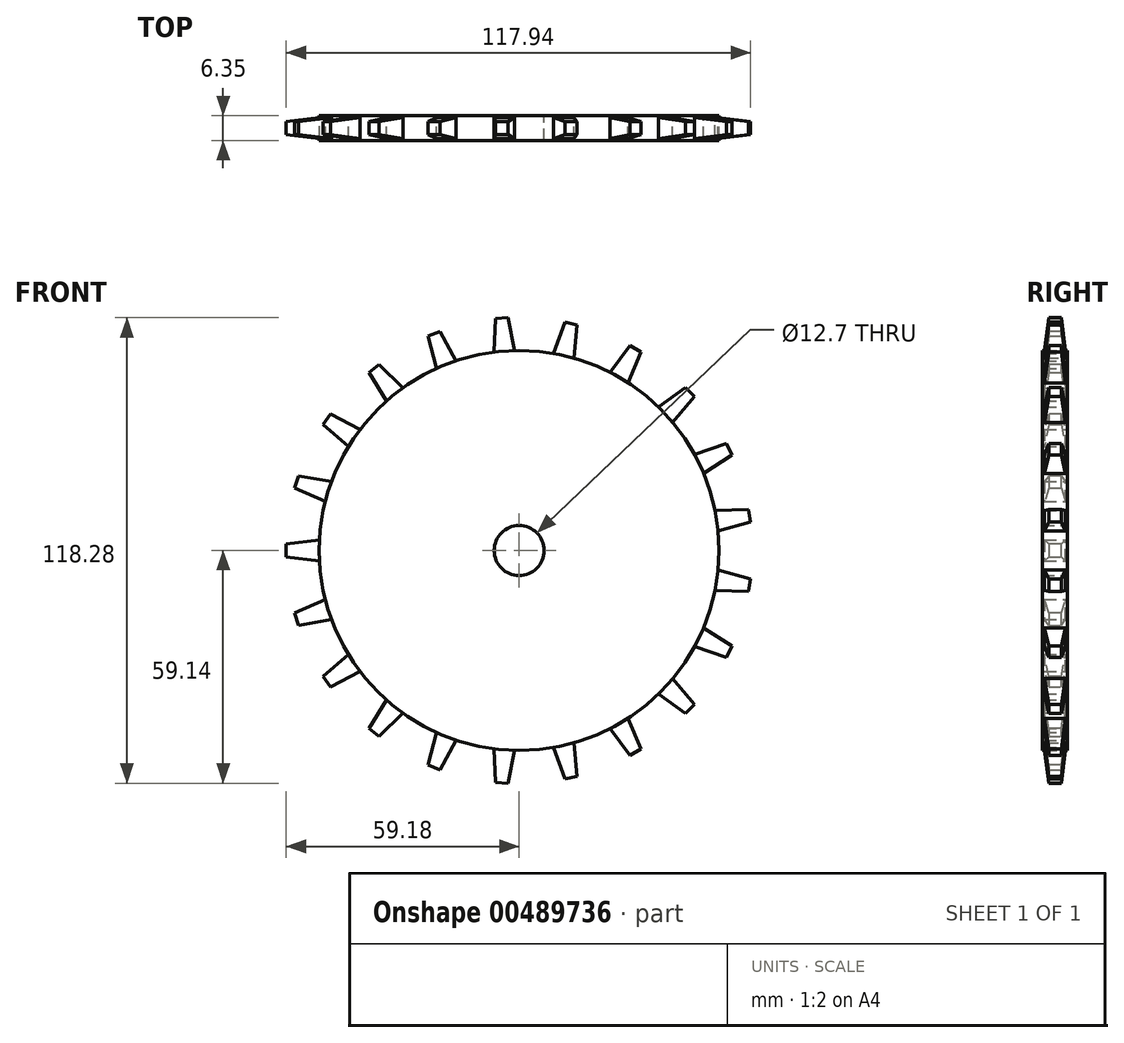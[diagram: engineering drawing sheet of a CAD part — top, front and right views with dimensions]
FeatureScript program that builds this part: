
annotation { "Feature Type Name" : "Feature", "Feature Type Description" : "" }
export const myFeature = defineFeature(function(context is Context, id is Id, definition is map)
    precondition{}
    {
        {
            var Q0;
            Q0=qCreatedBy(makeId("Front.planeOp"),FACE);
            var sketch = newSketch(context, id + "F0", { "sketchPlane" : qUnion([Q0])});
            skCircle(sketch, "E0", {"center": v(0, 0) * mm, "radius": 50.8 * mm});
            skCircle(sketch, "E1", {"center": v(0, 0) * mm, "radius": 6.35 * mm});
            skLineSegment(sketch, "E2", {"start": v(-57.15, 0) * mm, "end": v(-57.15, 3.8) * mm});
            skLineSegment(sketch, "E3", {"start": v(-57.15, -3.81) * mm, "end": v(-57.15, 0) * mm});
            skLineSegment(sketch, "E4.1.2", {"start": v(-39.4, 41.4) * mm, "end": v(-36.63, 44.03) * mm});
            skLineSegment(sketch, "E4.1.3", {"start": v(-42.15, 38.78) * mm, "end": v(-39.4, 41.4) * mm});
            skLineSegment(sketch, "E4.2.2", {"start": v(2.85, 57.08) * mm, "end": v(6.65, 56.89) * mm});
            skLineSegment(sketch, "E4.2.3", {"start": v(-0.96, 57.27) * mm, "end": v(2.85, 57.08) * mm});
            skLineSegment(sketch, "E4.3.2", {"start": v(43.32, 37.28) * mm, "end": v(45.8, 34.4) * mm});
            skLineSegment(sketch, "E4.3.3", {"start": v(40.83, 40.17) * mm, "end": v(43.32, 37.28) * mm});
            skLineSegment(sketch, "E4.4.2", {"start": v(56.87, -5.7) * mm, "end": v(56.49, -9.48) * mm});
            skLineSegment(sketch, "E4.4.3", {"start": v(57.25, -1.9) * mm, "end": v(56.87, -5.7) * mm});
            skLineSegment(sketch, "E4.5.2", {"start": v(35.07, -45.12) * mm, "end": v(32.06, -47.46) * mm});
            skLineSegment(sketch, "E4.5.3", {"start": v(38.08, -42.78) * mm, "end": v(35.07, -45.12) * mm});
            skLineSegment(sketch, "E4.6.2", {"start": v(-8.52, -56.51) * mm, "end": v(-12.29, -55.94) * mm});
            skLineSegment(sketch, "E4.6.3", {"start": v(-4.75, -57.08) * mm, "end": v(-8.52, -56.51) * mm});
            skLineSegment(sketch, "E4.7.2", {"start": v(-46.81, -32.78) * mm, "end": v(-49, -29.66) * mm});
            skLineSegment(sketch, "E4.7.3", {"start": v(-44.63, -35.9) * mm, "end": v(-46.81, -32.78) * mm});
            skSolve(sketch);
        }
        {
            var Q0;
            Q0 = qSketchRegion(id + "F0", true);
            var Q1;
            {var subQ0=sQuery(id+"F0.wireOp",EDGE,"E4.7.0");var subQ1=sQuery(id+"F0.wireOp",EDGE,"E1");var subQ2=makeQuery(id+"F0.imprint","INTERSECT",VERTEX,{"derivedFrom":[subQ1,subQ0]});Q1=makeQuery(id+"F0.imprint","IMPRINT",FACE,{"disambiguationData":[TD([[makeQuery(id+"F0.imprint","IMPRINT",EDGE,{"disambiguationData":[TD([[subQ2,-1.0]])],"derivedFrom":subQ1}),-1.0]])]});}
            var Q2;
            {var subQ0=sQuery(id+"F0.wireOp",EDGE,"55mzpF7p-MuUW-aDjL-x8Cu-YddlOPHiesim");var subQ1=sQuery(id+"F0.wireOp",EDGE,"E1");var subQ2=makeQuery(id+"F0.imprint","INTERSECT",VERTEX,{"derivedFrom":[subQ1,subQ0]});Q2=makeQuery(id+"F0.imprint","IMPRINT",FACE,{"disambiguationData":[TD([[makeQuery(id+"F0.imprint","IMPRINT",EDGE,{"disambiguationData":[TD([[subQ2,-1.0]])],"derivedFrom":subQ1}),-1.0]])]});}
            var Q3;
            {var subQ0=sQuery(id+"F0.wireOp",EDGE,"E4.1.0");var subQ1=sQuery(id+"F0.wireOp",EDGE,"E1");var subQ2=makeQuery(id+"F0.imprint","INTERSECT",VERTEX,{"derivedFrom":[subQ1,subQ0]});Q3=makeQuery(id+"F0.imprint","IMPRINT",FACE,{"disambiguationData":[TD([[makeQuery(id+"F0.imprint","IMPRINT",EDGE,{"disambiguationData":[TD([[subQ2,-1.0]])],"derivedFrom":subQ1}),-1.0]])]});}
            var Q4;
            {var subQ0=sQuery(id+"F0.wireOp",EDGE,"E4.2.0");var subQ1=sQuery(id+"F0.wireOp",EDGE,"E1");var subQ2=makeQuery(id+"F0.imprint","INTERSECT",VERTEX,{"derivedFrom":[subQ1,subQ0]});Q4=makeQuery(id+"F0.imprint","IMPRINT",FACE,{"disambiguationData":[TD([[makeQuery(id+"F0.imprint","IMPRINT",EDGE,{"disambiguationData":[TD([[subQ2,-1.0]])],"derivedFrom":subQ1}),-1.0]])]});}
            var Q5;
            {var subQ0=sQuery(id+"F0.wireOp",EDGE,"E4.4.1");var subQ1=sQuery(id+"F0.wireOp",EDGE,"E1");var subQ2=makeQuery(id+"F0.imprint","INTERSECT",VERTEX,{"derivedFrom":[subQ1,subQ0]});Q5=makeQuery(id+"F0.imprint","IMPRINT",FACE,{"disambiguationData":[TD([[makeQuery(id+"F0.imprint","IMPRINT",EDGE,{"disambiguationData":[TD([[subQ2,1.0]])],"derivedFrom":subQ1}),-1.0]])]});}
            var Q6;
            {var subQ0=sQuery(id+"F0.wireOp",EDGE,"E4.4.0");var subQ1=sQuery(id+"F0.wireOp",EDGE,"E1");var subQ2=makeQuery(id+"F0.imprint","INTERSECT",VERTEX,{"derivedFrom":[subQ1,subQ0]});Q6=makeQuery(id+"F0.imprint","IMPRINT",FACE,{"disambiguationData":[TD([[makeQuery(id+"F0.imprint","IMPRINT",EDGE,{"disambiguationData":[TD([[subQ2,-1.0]])],"derivedFrom":subQ1}),-1.0]])]});}
            var Q7;
            {var subQ0=sQuery(id+"F0.wireOp",EDGE,"E4.5.0");var subQ1=sQuery(id+"F0.wireOp",EDGE,"E1");var subQ2=makeQuery(id+"F0.imprint","INTERSECT",VERTEX,{"derivedFrom":[subQ1,subQ0]});Q7=makeQuery(id+"F0.imprint","IMPRINT",FACE,{"disambiguationData":[TD([[makeQuery(id+"F0.imprint","IMPRINT",EDGE,{"disambiguationData":[TD([[subQ2,-1.0]])],"derivedFrom":subQ1}),-1.0]])]});}
            var Q8;
            {var subQ0=sQuery(id+"F0.wireOp",EDGE,"E4.6.0");var subQ1=sQuery(id+"F0.wireOp",EDGE,"E1");var subQ2=makeQuery(id+"F0.imprint","INTERSECT",VERTEX,{"derivedFrom":[subQ1,subQ0]});Q8=makeQuery(id+"F0.imprint","IMPRINT",FACE,{"disambiguationData":[TD([[makeQuery(id+"F0.imprint","IMPRINT",EDGE,{"disambiguationData":[TD([[subQ2,-1.0]])],"derivedFrom":subQ1}),-1.0]])]});}
            extrude(context, id + "F1", {"entities" : qUnion([Q0, Q1, Q2, Q3, Q4, Q5, Q6, Q7, Q8]), "depth" : 6.35 * mm});
        }
        {
            var Q0;
            Q0=qCreatedBy(makeId("Right.planeOp"),FACE);
            cPlane(context, id + "F2", {"entities" : qUnion([Q0]), "cplaneType" : CPlaneType.OFFSET, "offset" : 46.48 * mm, "oppositeDirection" : true, "width" : 152.4 * mm, "height" : 152.4 * mm});
        }
        {
            var Q0;
            Q0=qCreatedBy(id+"F2.planeOp",FACE);
            var sketch = newSketch(context, id + "F3", { "sketchPlane" : qUnion([Q0])});
            skLineSegment(sketch, "E5", {"start": v(-6.35, 0) * mm, "end": v(-6.35, 3.17) * mm});
            skLineSegment(sketch, "E6", {"start": v(-6.35, 3.17) * mm, "end": v(0, 3.17) * mm});
            skLineSegment(sketch, "E7", {"start": v(0, 3.17) * mm, "end": v(0, -3.18) * mm});
            skLineSegment(sketch, "E8", {"start": v(0, -3.18) * mm, "end": v(-6.35, -3.18) * mm});
            skLineSegment(sketch, "E9", {"start": v(-6.35, -3.18) * mm, "end": v(-6.35, 0) * mm});
            skSolve(sketch);
        }
        {
            var Q0;
            Q0=makeQuery(id+"F3.imprint","IMPRINT",FACE,{"disambiguationData":[TD([[makeQuery(id+"F3.imprint","IMPRINT",EDGE,{"derivedFrom":sQuery(id+"F3.wireOp",EDGE,"E5")}),-1.0]])]});
            extrude(context, id + "F4", {"entities" : qUnion([Q0]), "operationType" : NewBodyOperationType.ADD, "oppositeDirection" : true, "depth" : 12.7 * mm, "hasDraft" : true, "draftAngle" : 7 * degree, "draftPullDirection" : true});
        }
        {
            var Q0;
            Q0=qCreatedBy(makeId("Right.planeOp"),FACE);
            var sketch = newSketch(context, id + "F5", { "sketchPlane" : qUnion([Q0])});
            skLineSegment(sketch, "E10", {"start": v(0, 0) * mm, "end": v(-61.18, 0) * mm});
            skSolve(sketch);
        }
        {
            var Q0;
            Q0=makeQuery(id+"F1.opExtrude","SWEPT_BODY",BODY,{"disambiguationData":[OSD([sQuery(id+"F0.wireOp",EDGE,"E0"),sQuery(id+"F0.wireOp",EDGE,"E1")])]});
            var Q1;
            Q1=sQuery(id+"F5.wireOp",EDGE,"E10");
            circularPattern(context, id + "F6", {"operationType" : NewBodyOperationType.ADD, "entities" : qUnion([Q0]), "axis" : qUnion([Q1]), "angle" : 360 * degree, "instanceCount" : 21, "equalSpace" : true});
        }
    });
